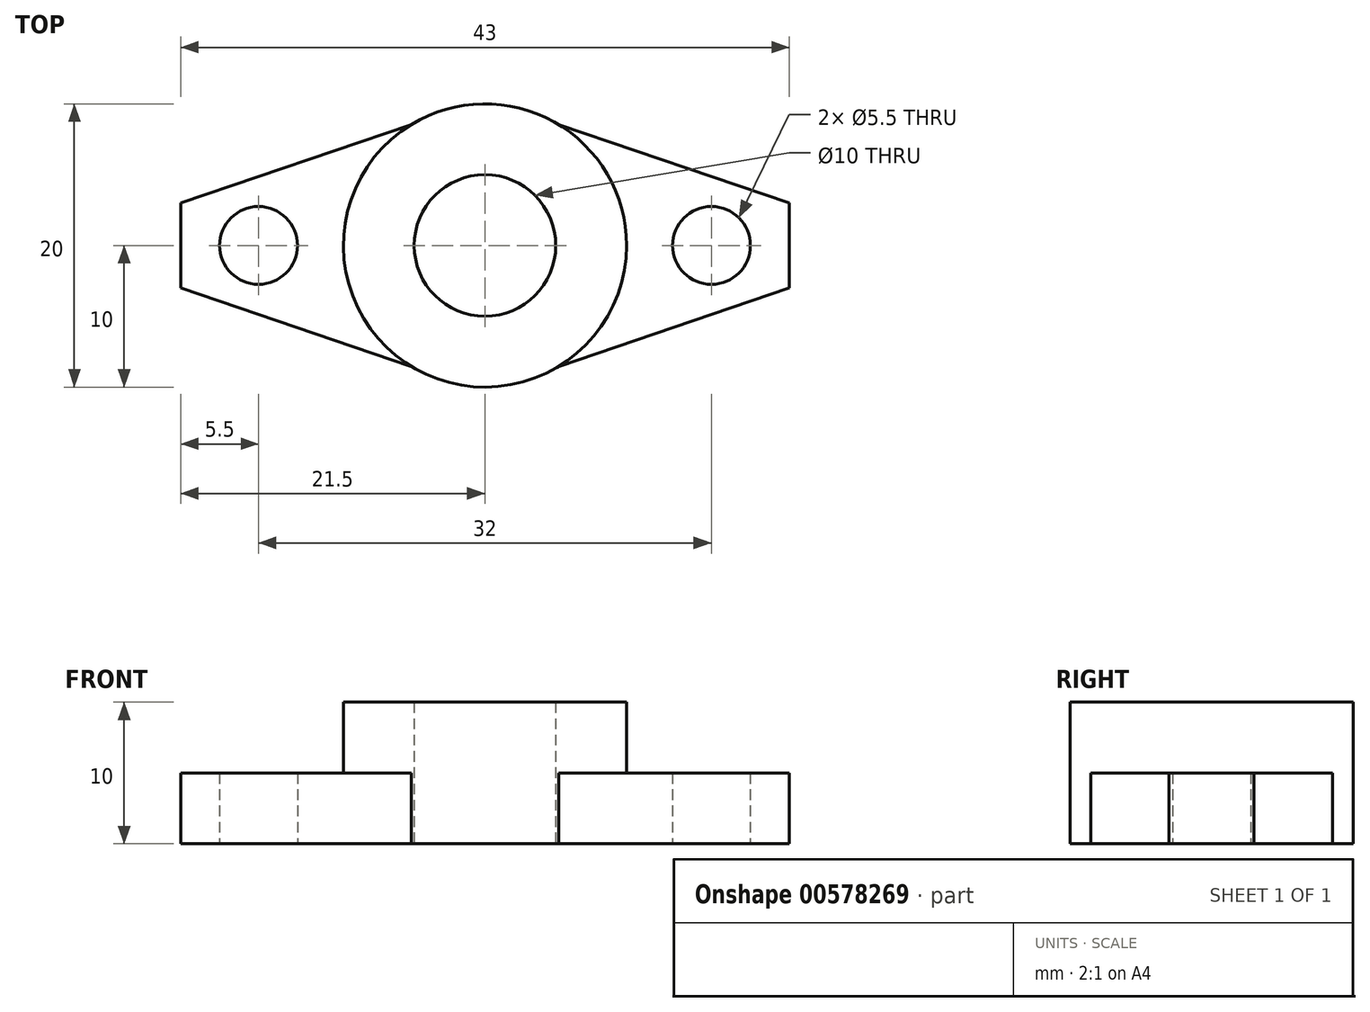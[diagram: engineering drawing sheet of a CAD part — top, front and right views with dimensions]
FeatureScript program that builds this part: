
annotation { "Feature Type Name" : "Feature", "Feature Type Description" : "" }
export const myFeature = defineFeature(function(context is Context, id is Id, definition is map)
    precondition{}
    {
        {
            var Q0;
            Q0=qCreatedBy(makeId("Top.planeOp"),FACE);
            var sketch = newSketch(context, id + "F0", { "sketchPlane" : qUnion([Q0])});
            skCircle(sketch, "E0", {"center": v(0, 0) * mm, "radius": 10 * mm});
            skCircle(sketch, "E1", {"center": v(0, 0) * mm, "radius": 5 * mm});
            skCircle(sketch, "E2", {"center": v(16, 0) * mm, "radius": 2.75 * mm});
            skCircle(sketch, "E3", {"center": v(-16, 0) * mm, "radius": 2.75 * mm});
            skLineSegment(sketch, "E4", {"start": v(-5.2, 8.55) * mm, "end": v(-21.5, 3) * mm});
            skLineSegment(sketch, "E5.MirrorCS", {"start": v(-5.2, -8.55) * mm, "end": v(-21.5, -3) * mm});
            skLineSegment(sketch, "E6", {"start": v(-21.5, 3) * mm, "end": v(-21.5, -3) * mm});
            skLineSegment(sketch, "E7.MirrorCS", {"start": v(5.2, 8.55) * mm, "end": v(21.5, 3) * mm});
            skLineSegment(sketch, "E8.MirrorCS", {"start": v(21.5, 3) * mm, "end": v(21.5, -3) * mm});
            skLineSegment(sketch, "E9.MirrorCS", {"start": v(5.2, -8.55) * mm, "end": v(21.5, -3) * mm});
            skSolve(sketch);
        }
        {
            var Q0;
            Q0=makeQuery(id+"F0.imprint","IMPRINT",FACE,{"disambiguationData":[TD([[makeQuery(id+"F0.imprint","IMPRINT",EDGE,{"derivedFrom":sQuery(id+"F0.wireOp",EDGE,"E1")}),-1.0]])]});
            extrude(context, id + "F1", {"entities" : qUnion([Q0]), "depth" : 10 * mm, "offsetDistance" : 25 * mm});
        }
        {
            var Q0;
            Q0=makeQuery(id+"F0.imprint","IMPRINT",FACE,{"disambiguationData":[TD([[makeQuery(id+"F0.imprint","IMPRINT",EDGE,{"derivedFrom":sQuery(id+"F0.wireOp",EDGE,"E3")}),-1.0]])]});
            var Q1;
            Q1=makeQuery(id+"F0.imprint","IMPRINT",FACE,{"disambiguationData":[TD([[makeQuery(id+"F0.imprint","IMPRINT",EDGE,{"derivedFrom":sQuery(id+"F0.wireOp",EDGE,"E2")}),-1.0]])]});
            extrude(context, id + "F2", {"entities" : qUnion([Q0, Q1]), "operationType" : NewBodyOperationType.ADD, "depth" : 5 * mm, "offsetDistance" : 25 * mm});
        }
    });
